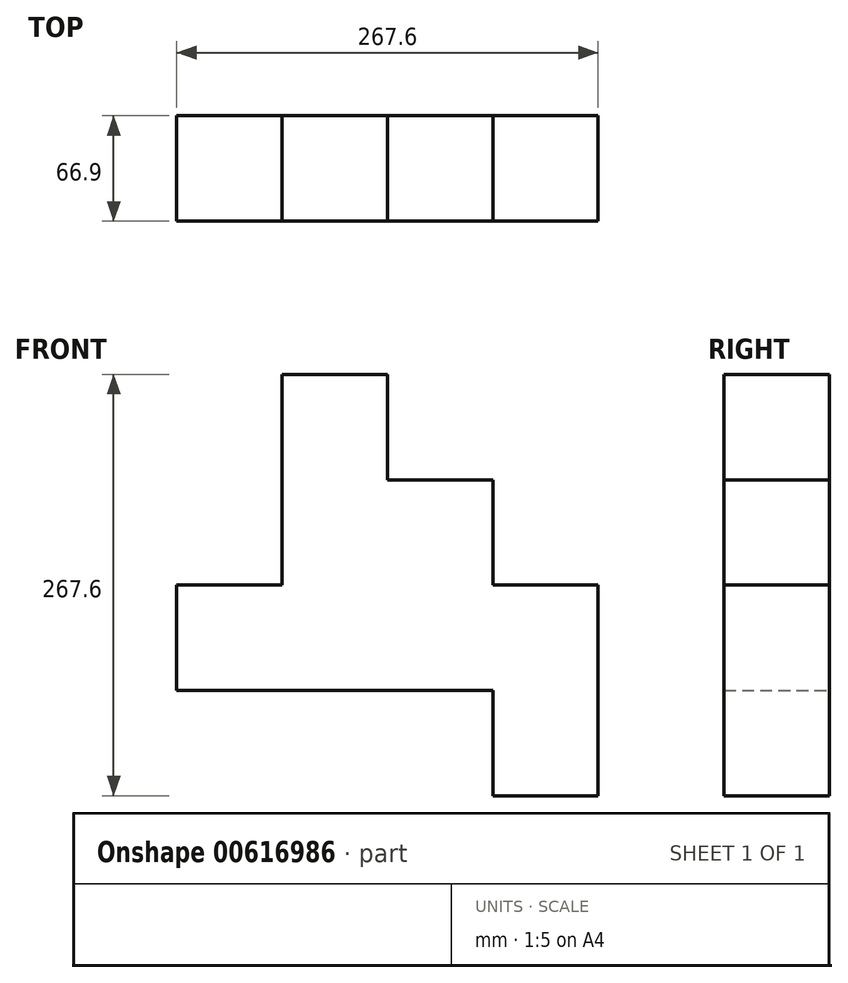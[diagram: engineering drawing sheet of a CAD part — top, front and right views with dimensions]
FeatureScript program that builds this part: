
annotation { "Feature Type Name" : "Feature", "Feature Type Description" : "" }
export const myFeature = defineFeature(function(context is Context, id is Id, definition is map)
    precondition{}
    {
        {
            var Q0;
            Q0=qCreatedBy(makeId("Front.planeOp"),FACE);
            var sketch = newSketch(context, id + "F0", { "sketchPlane" : qUnion([Q0])});
            skLineSegment(sketch, "E0", {"start": v(-74.57, 175.54) * mm, "end": v(-7.67, 175.54) * mm});
            skLineSegment(sketch, "E1", {"start": v(-7.67, 175.54) * mm, "end": v(-7.67, 108.64) * mm});
            skLineSegment(sketch, "E2", {"start": v(-7.67, 108.64) * mm, "end": v(59.23, 108.64) * mm});
            skLineSegment(sketch, "E3", {"start": v(59.23, 108.64) * mm, "end": v(59.23, 41.74) * mm});
            skLineSegment(sketch, "E4", {"start": v(59.23, 41.74) * mm, "end": v(126.13, 41.74) * mm});
            skLineSegment(sketch, "E5", {"start": v(126.13, 41.74) * mm, "end": v(126.13, -92.06) * mm});
            skLineSegment(sketch, "E6", {"start": v(126.13, -92.06) * mm, "end": v(59.23, -92.06) * mm});
            skLineSegment(sketch, "E7", {"start": v(59.23, -92.06) * mm, "end": v(59.23, -25.16) * mm});
            skLineSegment(sketch, "E8", {"start": v(59.23, -25.16) * mm, "end": v(-141.47, -25.16) * mm});
            skLineSegment(sketch, "E9", {"start": v(-141.47, 41.74) * mm, "end": v(-141.47, -25.16) * mm});
            skLineSegment(sketch, "E10", {"start": v(-141.47, 41.74) * mm, "end": v(-74.57, 41.74) * mm});
            skLineSegment(sketch, "E11", {"start": v(-74.57, 41.74) * mm, "end": v(-74.57, 175.54) * mm});
            skSolve(sketch);
        }
        {
            var Q0;
            Q0=makeQuery(id+"F0.imprint","IMPRINT",FACE,{"disambiguationData":[TD([[makeQuery(id+"F0.imprint","IMPRINT",EDGE,{"derivedFrom":sQuery(id+"F0.wireOp",EDGE,"E0")}),-1.0]])]});
            extrude(context, id + "F1", {"entities" : qUnion([Q0]), "depth" : 66.9 * mm, "offsetDistance" : 25 * mm});
        }
    });
